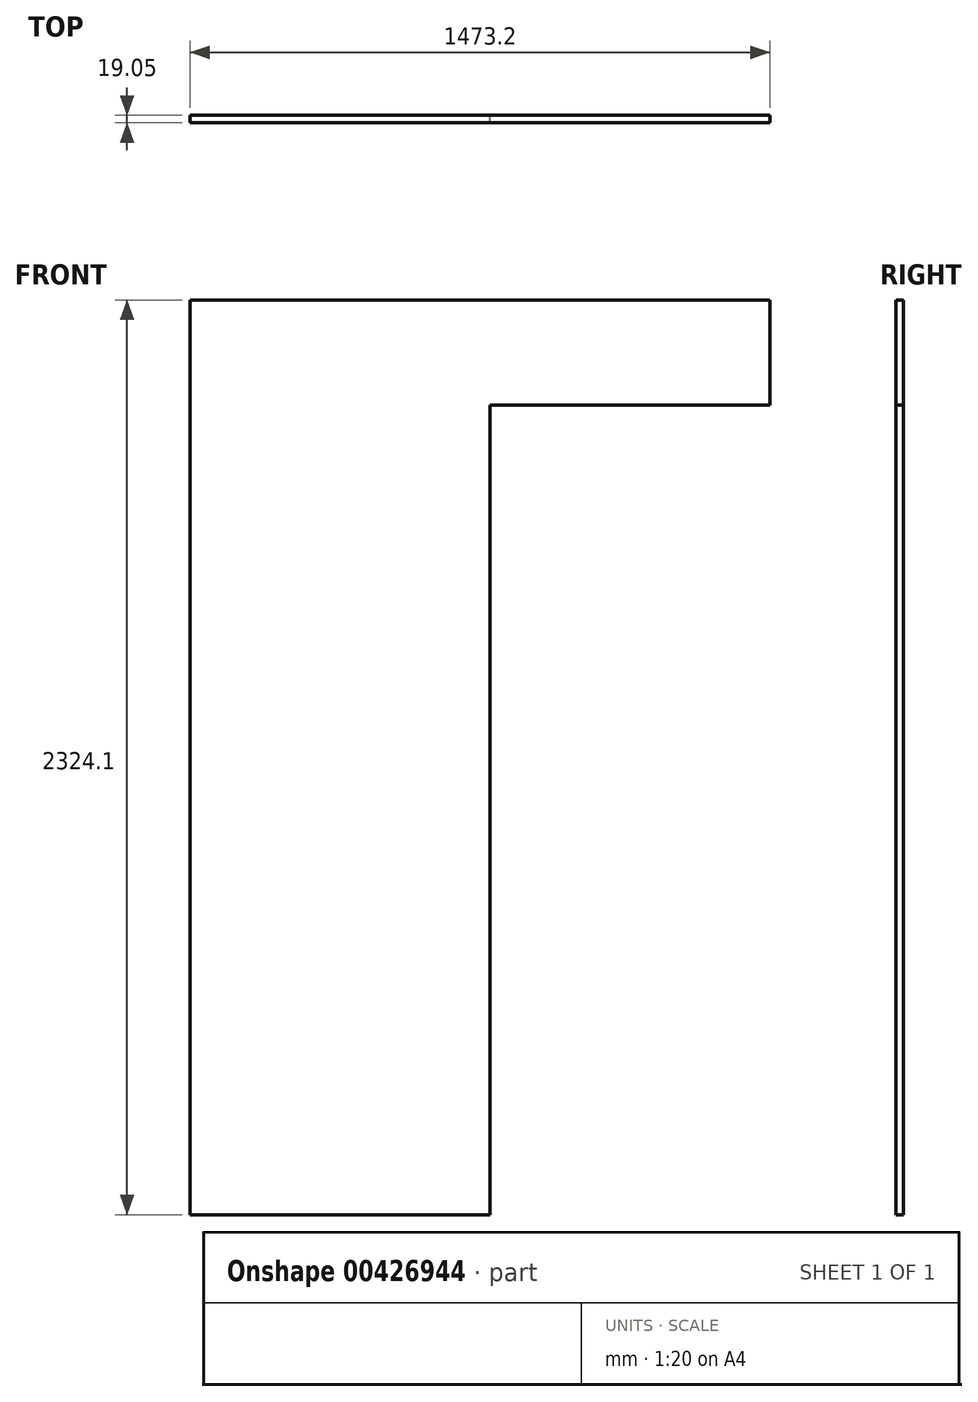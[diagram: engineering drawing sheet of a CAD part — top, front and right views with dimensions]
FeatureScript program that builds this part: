
annotation { "Feature Type Name" : "Feature", "Feature Type Description" : "" }
export const myFeature = defineFeature(function(context is Context, id is Id, definition is map)
    precondition{}
    {
        {
            var Q0;
            Q0=qCreatedBy(makeId("Front.planeOp"),FACE);
            var sketch = newSketch(context, id + "F0", { "sketchPlane" : qUnion([Q0])});
            skLineSegment(sketch, "E0", {"start": v(0, 0) * mm, "end": v(0, 2324.1) * mm});
            skLineSegment(sketch, "E1", {"start": v(0, 2324.1) * mm, "end": v(1473.2, 2324.1) * mm});
            skLineSegment(sketch, "E2", {"start": v(1473.2, 2324.1) * mm, "end": v(1473.2, 2057.4) * mm});
            skLineSegment(sketch, "E3", {"start": v(1473.2, 2057.4) * mm, "end": v(762, 2057.4) * mm});
            skLineSegment(sketch, "E4", {"start": v(762, 2057.4) * mm, "end": v(762, 0) * mm});
            skLineSegment(sketch, "E5", {"start": v(762, 0) * mm, "end": v(0, 0) * mm});
            skSolve(sketch);
        }
        {
            var Q0;
            Q0=makeQuery(id+"F0.imprint","IMPRINT",FACE,{"disambiguationData":[TD([[makeQuery(id+"F0.imprint","IMPRINT",EDGE,{"derivedFrom":sQuery(id+"F0.wireOp",EDGE,"E0")}),-1.0]])]});
            extrude(context, id + "F1", {"entities" : qUnion([Q0]), "depth" : 19.05 * mm});
        }
    });
